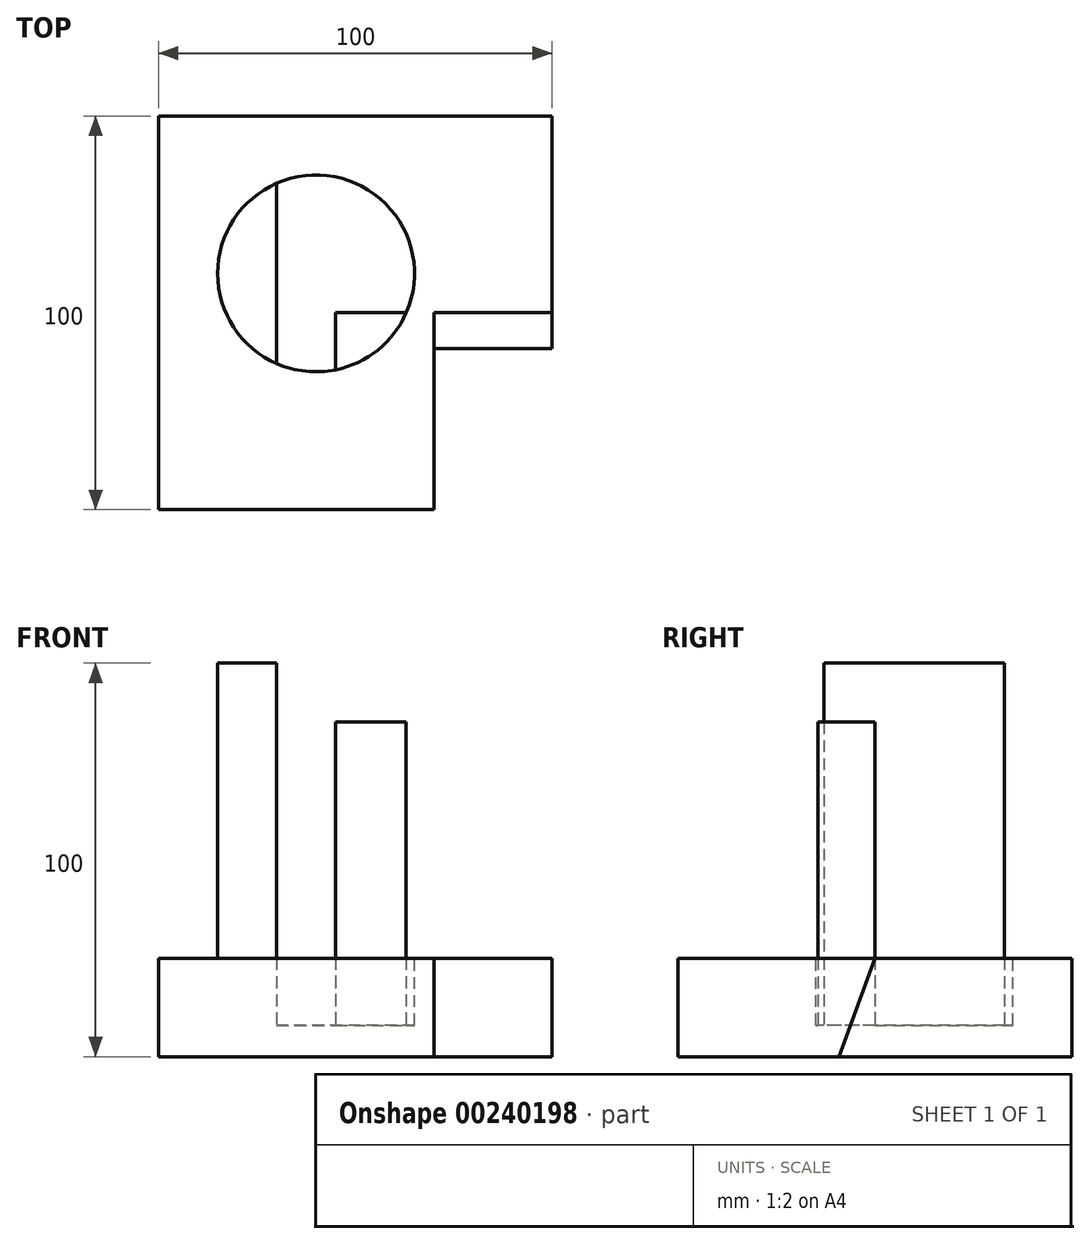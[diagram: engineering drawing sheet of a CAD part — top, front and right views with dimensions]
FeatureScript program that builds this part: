
annotation { "Feature Type Name" : "Feature", "Feature Type Description" : "" }
export const myFeature = defineFeature(function(context is Context, id is Id, definition is map)
    precondition{}
    {
        {
            var Q0;
            Q0=qCreatedBy(makeId("Front.planeOp"),FACE);
            var sketch = newSketch(context, id + "F0", { "sketchPlane" : qUnion([Q0])});
            skLineSegment(sketch, "E0.bottom", {"start": v(0, 0) * mm, "end": v(100, 0) * mm});
            skLineSegment(sketch, "E0.top", {"start": v(0, 100) * mm, "end": v(100, 100) * mm});
            skLineSegment(sketch, "E0.left", {"start": v(0, 0) * mm, "end": v(0, 100) * mm});
            skLineSegment(sketch, "E0.right", {"start": v(100, 0) * mm, "end": v(100, 100) * mm});
            skSolve(sketch);
        }
        {
            var Q0;
            Q0 = qSketchRegion(id + "F0", true);
            extrude(context, id + "F1", {"entities" : qUnion([Q0]), "oppositeDirection" : true, "depth" : 100 * mm});
        }
        {
            var Q0;
            Q0=makeQuery(id+"F1.opExtrude","SWEPT_FACE",FACE,{"disambiguationData":[OSD([sQuery(id+"F0.wireOp",EDGE,"E0.right")])]});
            var sketch = newSketch(context, id + "F2", { "sketchPlane" : qUnion([Q0])});
            skLineSegment(sketch, "E1.bottom", {"start": v(0, 100) * mm, "end": v(100, 100) * mm});
            skLineSegment(sketch, "E1.top", {"start": v(0, 25) * mm, "end": v(100, 25) * mm});
            skLineSegment(sketch, "E1.left", {"start": v(0, 100) * mm, "end": v(0, 25) * mm});
            skLineSegment(sketch, "E1.right", {"start": v(100, 100) * mm, "end": v(100, 25) * mm});
            skSolve(sketch);
        }
        {
            var Q0;
            Q0 = qSketchRegion(id + "F2", true);
            extrude(context, id + "F3", {"entities" : qUnion([Q0]), "operationType" : NewBodyOperationType.REMOVE, "endBound" : BoundingType.THROUGH_ALL, "oppositeDirection" : true, "depth" : 25 * mm});
        }
        {
            var Q0;
            Q0=makeQuery(id+"F3.boolean.opBoolean","COPY",FACE,{"derivedFrom":makeQuery(id+"F3.opExtrude","SWEPT_FACE",FACE,{"disambiguationData":[OSD([sQuery(id+"F2.wireOp",EDGE,"E1.top")])]})});
            var sketch = newSketch(context, id + "F4", { "sketchPlane" : qUnion([Q0])});
            skCircle(sketch, "E2", {"center": v(40, 60) * mm, "radius": 25 * mm});
            skSolve(sketch);
        }
        {
            var Q0;
            Q0 = qSketchRegion(id + "F4", true);
            extrude(context, id + "F5", {"entities" : qUnion([Q0]), "operationType" : NewBodyOperationType.REMOVE, "oppositeDirection" : true, "depth" : 17 * mm});
        }
        {
            var Q0;
            Q0=makeQuery(id+"F5.boolean.opBoolean","COPY",FACE,{"derivedFrom":makeQuery(id+"F5.opExtrude","CAP_FACE",FACE,{"disambiguationData":[OSD([sQuery(id+"F4.wireOp",EDGE,"E2")])],"isStart":false})});
            var sketch = newSketch(context, id + "F6", { "sketchPlane" : qUnion([Q0])});
            skLineSegment(sketch, "E3", {"start": v(30, 82.91) * mm, "end": v(30, 37.09) * mm});
            skLineSegment(sketch, "E4", {"start": v(45, 50) * mm, "end": v(45, 35.5) * mm});
            skArc(sketch, "E5", {"start": v(30, 82.91) * mm, "mid": v(15, 60) * mm, "end": v(30, 37.09) * mm});
            skArc(sketch, "E6", {"start": v(45, 35.5) * mm, "mid": v(65, 60) * mm, "end": v(45, 84.5) * mm});
            skLineSegment(sketch, "E7", {"start": v(45, 50) * mm, "end": v(62.91, 50) * mm});
            skSolve(sketch);
        }
        {
            var Q0;
            Q0 = qSketchRegion(id + "F6", true);
            extrude(context, id + "F7", {"entities" : qUnion([Q0]), "operationType" : NewBodyOperationType.ADD, "depth" : (100 - 25 + 17) * mm});
        }
        {
            var Q0;
            Q0=makeQuery(id+"F1.opExtrude","CAP_FACE",FACE,{"disambiguationData":[OSD([sQuery(id+"F0.wireOp",EDGE,"E0.bottom"),sQuery(id+"F0.wireOp",EDGE,"E0.top"),sQuery(id+"F0.wireOp",EDGE,"E0.left"),sQuery(id+"F0.wireOp",EDGE,"E0.right")])],"isStart":true});
            var sketch = newSketch(context, id + "F8", { "sketchPlane" : qUnion([Q0])});
            skLineSegment(sketch, "E8.bottom", {"start": v(38.94, 117.92) * mm, "end": v(69.71, 117.92) * mm});
            skLineSegment(sketch, "E8.top", {"start": v(38.94, 85) * mm, "end": v(69.71, 85) * mm});
            skLineSegment(sketch, "E8.left", {"start": v(38.94, 117.92) * mm, "end": v(38.94, 85) * mm});
            skLineSegment(sketch, "E8.right", {"start": v(69.71, 117.92) * mm, "end": v(69.71, 85) * mm});
            skSolve(sketch);
        }
        {
            var Q0;
            Q0 = qSketchRegion(id + "F8", true);
            extrude(context, id + "F9", {"entities" : qUnion([Q0]), "operationType" : NewBodyOperationType.REMOVE, "endBound" : BoundingType.THROUGH_ALL, "oppositeDirection" : true, "depth" : 25 * mm});
        }
        {
            var Q0;
            Q0=makeQuery(id+"F1.opExtrude","SWEPT_FACE",FACE,{"disambiguationData":[OSD([sQuery(id+"F0.wireOp",EDGE,"E0.right")])]});
            var sketch = newSketch(context, id + "F10", { "sketchPlane" : qUnion([Q0])});
            skLineSegment(sketch, "E9", {"start": v(50, 25) * mm, "end": v(40.9, 0) * mm});
            skLineSegment(sketch, "E10", {"start": v(40.9, 0) * mm, "end": v(0, 0) * mm});
            skLineSegment(sketch, "E11", {"start": v(0, 0) * mm, "end": v(0, 25) * mm});
            skLineSegment(sketch, "E12", {"start": v(0, 25) * mm, "end": v(50, 25) * mm});
            skSolve(sketch);
        }
        {
            var Q0;
            Q0 = qSketchRegion(id + "F10", true);
            extrude(context, id + "F11", {"entities" : qUnion([Q0]), "operationType" : NewBodyOperationType.REMOVE, "oppositeDirection" : true, "depth" : 30 * mm});
        }
    });
